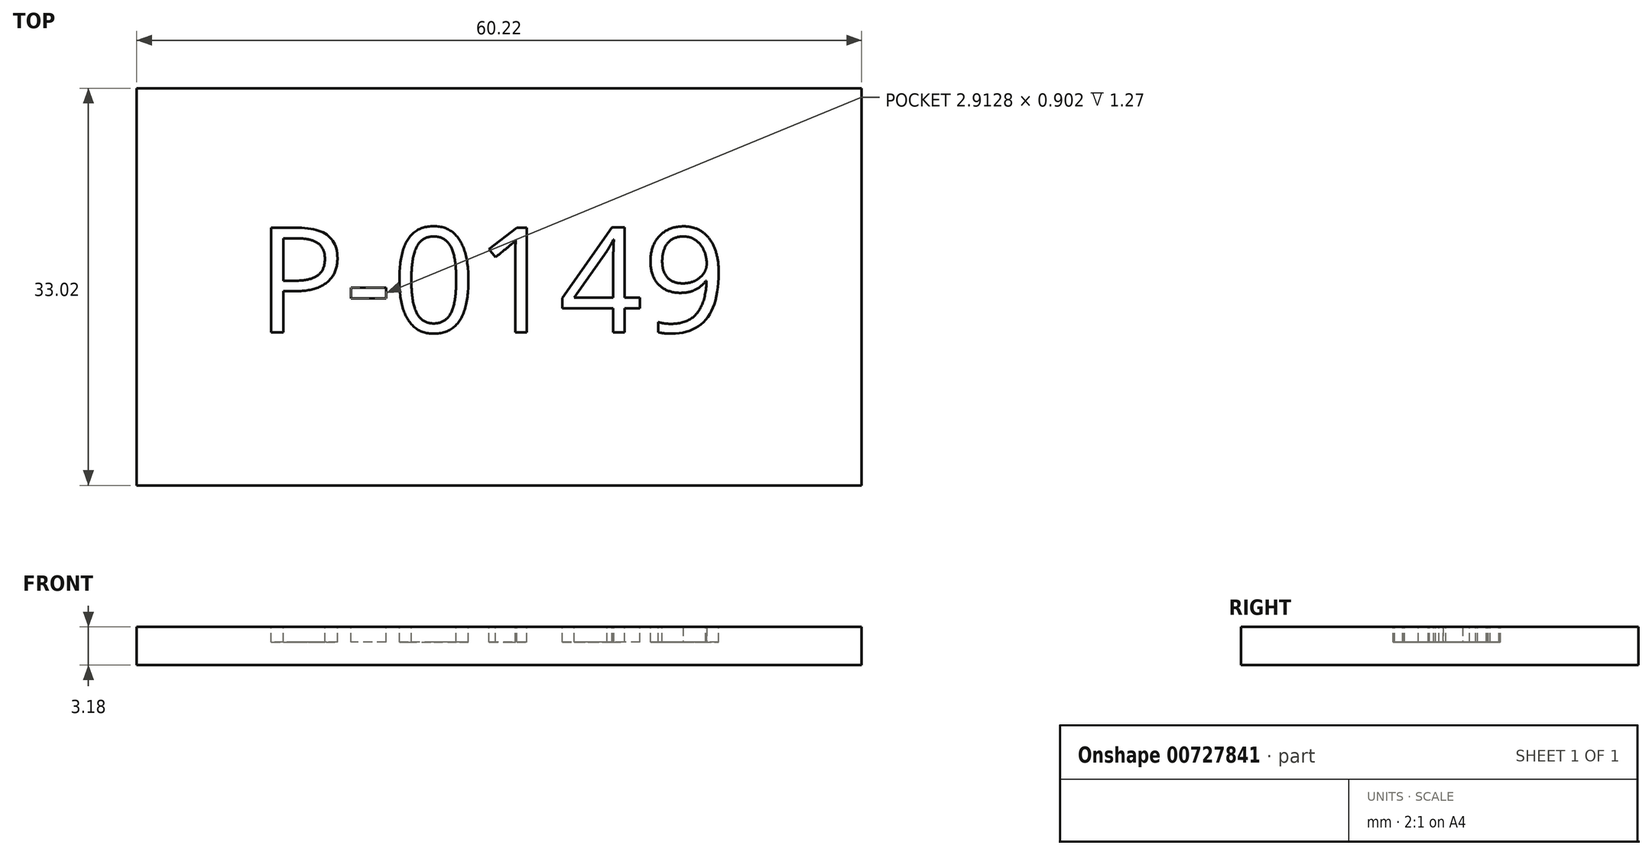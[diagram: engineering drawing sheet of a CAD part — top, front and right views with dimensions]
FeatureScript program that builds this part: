
annotation { "Feature Type Name" : "Feature", "Feature Type Description" : "" }
export const myFeature = defineFeature(function(context is Context, id is Id, definition is map)
    precondition{}
    {
        {
            var Q0;
            Q0=qCreatedBy(makeId("Top.planeOp"),FACE);
            var sketch = newSketch(context, id + "F0", { "sketchPlane" : qUnion([Q0])});
            skLineSegment(sketch, "E0.bottom", {"start": v(-6.96, -41.7) * mm, "end": v(53.26, -41.7) * mm});
            skLineSegment(sketch, "E0.top", {"start": v(-6.96, -8.68) * mm, "end": v(53.26, -8.68) * mm});
            skLineSegment(sketch, "E0.left", {"start": v(-6.96, -41.7) * mm, "end": v(-6.96, -8.68) * mm});
            skLineSegment(sketch, "E0.right", {"start": v(53.26, -41.7) * mm, "end": v(53.26, -8.68) * mm});
            skSolve(sketch);
        }
        {
            var Q0;
            Q0=makeQuery(id+"F0.imprint","IMPRINT",FACE,{"disambiguationData":[TD([[makeQuery(id+"F0.imprint","IMPRINT",EDGE,{"derivedFrom":sQuery(id+"F0.wireOp",EDGE,"E0.bottom")}),1.0]])]});
            extrude(context, id + "F1", {"entities" : qUnion([Q0]), "depth" : 3.17 * mm, "offsetDistance" : 25.4 * mm});
        }
        {
            var Q0;
            Q0=makeQuery(id+"F1.opExtrude","CAP_FACE",FACE,{"disambiguationData":[OSD([sQuery(id+"F0.wireOp",EDGE,"E0.bottom"),sQuery(id+"F0.wireOp",EDGE,"E0.top"),sQuery(id+"F0.wireOp",EDGE,"E0.left"),sQuery(id+"F0.wireOp",EDGE,"E0.right")])],"isStart":false});
            var sketch = newSketch(context, id + "F2", { "sketchPlane" : qUnion([Q0])});
            skText(sketch, "E1", { "text": "P-0149", "fontName": "OpenSans-Regular.ttf"});
            const initialGuessF2  = {"E1": [0.00303, -0.02896, 1, 0, 0.00875]};
            skSetInitialGuess(sketch, initialGuessF2);
            skSolve(sketch);
        }
        {
            var Q0;
            Q0 = qSketchRegion(id + "F2", true);
            extrude(context, id + "F3", {"entities" : qUnion([Q0]), "operationType" : NewBodyOperationType.REMOVE, "oppositeDirection" : true, "depth" : 1.27 * mm, "offsetDistance" : 25.4 * mm});
        }
    });
